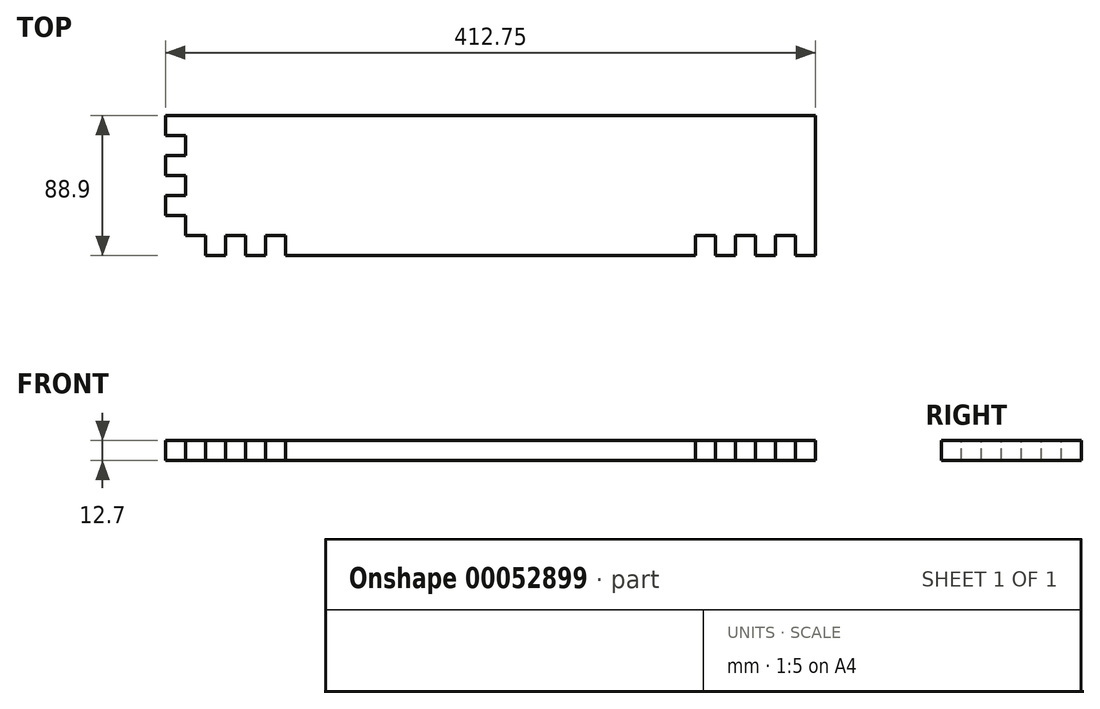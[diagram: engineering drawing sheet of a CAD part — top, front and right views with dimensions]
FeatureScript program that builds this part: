
annotation { "Feature Type Name" : "Feature", "Feature Type Description" : "" }
export const myFeature = defineFeature(function(context is Context, id is Id, definition is map)
    precondition{}
    {
        {
            var Q0;
            Q0=qCreatedBy(makeId("Top.planeOp"),FACE);
            var sketch = newSketch(context, id + "F0", { "sketchPlane" : qUnion([Q0])});
            skLineSegment(sketch, "E0.bottom", {"start": v(0, 0) * mm, "end": v(412.75, 0) * mm});
            skLineSegment(sketch, "E0.top", {"start": v(0, 88.9) * mm, "end": v(412.75, 88.9) * mm});
            skLineSegment(sketch, "E0.left", {"start": v(0, 0) * mm, "end": v(0, 88.9) * mm});
            skLineSegment(sketch, "E0.right", {"start": v(412.75, 0) * mm, "end": v(412.75, 88.9) * mm});
            skSolve(sketch);
        }
        {
            var Q0;
            Q0=qSketchRegion(id+"F0",true);
            extrude(context, id + "F1", {"entities" : qUnion([Q0]), "depth" : 12.7 * mm});
        }
        {
            var Q0;
            Q0=makeQuery(id+"F1.opExtrude","CAP_FACE",FACE,{"disambiguationData":[OSD([sQuery(id+"F0.wireOp",EDGE,"E0.bottom"),sQuery(id+"F0.wireOp",EDGE,"E0.top"),sQuery(id+"F0.wireOp",EDGE,"E0.left"),sQuery(id+"F0.wireOp",EDGE,"E0.right")])],"isStart":false});
            var sketch = newSketch(context, id + "F2", { "sketchPlane" : qUnion([Q0])});
            skLineSegment(sketch, "E1.top", {"start": v(0, 25.4) * mm, "end": v(12.7, 25.4) * mm});
            skLineSegment(sketch, "E1.left", {"start": v(0, 0) * mm, "end": v(0, 25.4) * mm});
            skLineSegment(sketch, "E1.right", {"start": v(12.7, 0) * mm, "end": v(12.7, 25.4) * mm});
            skLineSegment(sketch, "E2.bottom", {"start": v(0, 63.5) * mm, "end": v(12.7, 63.5) * mm});
            skLineSegment(sketch, "E2.top", {"start": v(0, 76.2) * mm, "end": v(12.7, 76.2) * mm});
            skLineSegment(sketch, "E2.left", {"start": v(0, 63.5) * mm, "end": v(0, 76.2) * mm});
            skLineSegment(sketch, "E2.right", {"start": v(12.7, 63.5) * mm, "end": v(12.7, 76.2) * mm});
            skLineSegment(sketch, "E3.bottom", {"start": v(0, 38.1) * mm, "end": v(12.7, 38.1) * mm});
            skLineSegment(sketch, "E3.top", {"start": v(0, 50.8) * mm, "end": v(12.7, 50.8) * mm});
            skLineSegment(sketch, "E3.left", {"start": v(0, 38.1) * mm, "end": v(0, 50.8) * mm});
            skLineSegment(sketch, "E3.right", {"start": v(12.7, 38.1) * mm, "end": v(12.7, 50.8) * mm});
            skLineSegment(sketch, "E4", {"start": v(0, 0) * mm, "end": v(12.7, 0) * mm});
            skSolve(sketch);
        }
        {
            var Q0;
            Q0=qSketchRegion(id+"F2",true);
            extrude(context, id + "F3", {"entities" : qUnion([Q0]), "operationType" : NewBodyOperationType.REMOVE, "oppositeDirection" : true, "depth" : 25.4 * mm});
        }
        {
            var Q0;
            Q0=makeQuery(id+"F1.opExtrude","CAP_FACE",FACE,{"disambiguationData":[OSD([sQuery(id+"F0.wireOp",EDGE,"E0.bottom"),sQuery(id+"F0.wireOp",EDGE,"E0.top"),sQuery(id+"F0.wireOp",EDGE,"E0.left"),sQuery(id+"F0.wireOp",EDGE,"E0.right")])],"isStart":false});
            var sketch = newSketch(context, id + "F4", { "sketchPlane" : qUnion([Q0])});
            skLineSegment(sketch, "E5.bottom", {"start": v(400.05, 0) * mm, "end": v(387.35, 0) * mm});
            skLineSegment(sketch, "E5.top", {"start": v(400.05, 12.7) * mm, "end": v(387.35, 12.7) * mm});
            skLineSegment(sketch, "E5.left", {"start": v(400.05, 0) * mm, "end": v(400.05, 12.7) * mm});
            skLineSegment(sketch, "E5.right", {"start": v(387.35, 0) * mm, "end": v(387.35, 12.7) * mm});
            skLineSegment(sketch, "E6.bottom", {"start": v(374.65, 0) * mm, "end": v(361.95, 0) * mm});
            skLineSegment(sketch, "E6.top", {"start": v(374.65, 12.7) * mm, "end": v(361.95, 12.7) * mm});
            skLineSegment(sketch, "E6.left", {"start": v(374.65, 0) * mm, "end": v(374.65, 12.7) * mm});
            skLineSegment(sketch, "E6.right", {"start": v(361.95, 0) * mm, "end": v(361.95, 12.7) * mm});
            skLineSegment(sketch, "E7.bottom", {"start": v(349.25, 0) * mm, "end": v(336.55, 0) * mm});
            skLineSegment(sketch, "E7.top", {"start": v(349.25, 12.7) * mm, "end": v(336.55, 12.7) * mm});
            skLineSegment(sketch, "E7.left", {"start": v(349.25, 0) * mm, "end": v(349.25, 12.7) * mm});
            skLineSegment(sketch, "E7.right", {"start": v(336.55, 0) * mm, "end": v(336.55, 12.7) * mm});
            skSolve(sketch);
        }
        {
            var Q0;
            Q0=qSketchRegion(id+"F4",true);
            extrude(context, id + "F5", {"entities" : qUnion([Q0]), "operationType" : NewBodyOperationType.REMOVE, "oppositeDirection" : true, "depth" : 25.4 * mm});
        }
        {
            var Q0;
            Q0=makeQuery(id+"F1.opExtrude","CAP_FACE",FACE,{"disambiguationData":[OSD([sQuery(id+"F0.wireOp",EDGE,"E0.bottom"),sQuery(id+"F0.wireOp",EDGE,"E0.top"),sQuery(id+"F0.wireOp",EDGE,"E0.left"),sQuery(id+"F0.wireOp",EDGE,"E0.right")])],"isStart":false});
            var sketch = newSketch(context, id + "F6", { "sketchPlane" : qUnion([Q0])});
            skLineSegment(sketch, "E8.bottom", {"start": v(12.7, 0) * mm, "end": v(25.4, 0) * mm});
            skLineSegment(sketch, "E8.top", {"start": v(12.7, 12.7) * mm, "end": v(25.4, 12.7) * mm});
            skLineSegment(sketch, "E8.left", {"start": v(12.7, 0) * mm, "end": v(12.7, 12.7) * mm});
            skLineSegment(sketch, "E8.right", {"start": v(25.4, 0) * mm, "end": v(25.4, 12.7) * mm});
            skLineSegment(sketch, "E9.bottom", {"start": v(38.1, 0) * mm, "end": v(50.8, 0) * mm});
            skLineSegment(sketch, "E9.top", {"start": v(38.1, 12.7) * mm, "end": v(50.8, 12.7) * mm});
            skLineSegment(sketch, "E9.left", {"start": v(38.1, 0) * mm, "end": v(38.1, 12.7) * mm});
            skLineSegment(sketch, "E9.right", {"start": v(50.8, 0) * mm, "end": v(50.8, 12.7) * mm});
            skLineSegment(sketch, "E10.bottom", {"start": v(63.5, 0) * mm, "end": v(76.2, 0) * mm});
            skLineSegment(sketch, "E10.top", {"start": v(63.5, 12.7) * mm, "end": v(76.2, 12.7) * mm});
            skLineSegment(sketch, "E10.left", {"start": v(63.5, 0) * mm, "end": v(63.5, 12.7) * mm});
            skLineSegment(sketch, "E10.right", {"start": v(76.2, 0) * mm, "end": v(76.2, 12.7) * mm});
            skSolve(sketch);
        }
        {
            var Q0;
            Q0 = qSketchRegion(id + "F6", true);
            extrude(context, id + "F7", {"entities" : qUnion([Q0]), "operationType" : NewBodyOperationType.REMOVE, "oppositeDirection" : true, "depth" : 25.4 * mm});
        }
    });
